# Revit family: Hager-UNIVERS-Surface_mounted-IP44-With_Cover-With_DIN-NoHosted-PL-pl
name_source: partatom
category: Electrical Equipment
units: mm (PartAtom-declared; Revit-internal decimal feet)

## family parameters
Always vertical = Yes
Cut with Voids When Loaded = No
Maintain Annotation Orientation = No
Panel Configuration = Two Columns, Circuits Across
Part Type = Panelboard
Room Calculation Point = No
Round Connector Dimension = Use Diameter
Shared = No
Work Plane-Based = Yes

## types (33) — shared parameters
Code hager = ADD-EC000214_EU
Default Elevation = 1200 mm
EF000007 - Kolor = Biały
EF000024 - Odporność na promieniowanie UV = No
EF000049 - Głębokość = 165 mm
EF000116 - Numer RAL = 9010
EF000118 - Z płytą montażową = No
EF000218 - Głębokość wbudowania = 161 mm  [stored 0.528215 ft]
EF001062 - Wykonanie zgodne z Dyrektywą Kompatybilności Elektromagnetycznej EMC = No
EF001088 - Możliwość rozbudowy = Yes
EF001134 - Szyna DIN = Yes
EF004462 - Rodzaj zamknięcia = Inne
EF005474 - Stopień ochrony (IP) = IP44
EF006244 - Transparentna pokrywa/drzwi = No
EF006306 - Z zamkiem = No
EF015941 - Drzwi przepuszczające sygnał = No
ETIM class code = EC000214
ETIM class name = Small distribution board
HG000002-with door or cover-pl = Yes
HG000003-Range-pl = UNIVERS
HG000005-Thickness-pl = 2 mm  [stored 0.00656168 ft]
HG000006-Flush mounted-pl = No
HG000011-Empty rows from bottom-pl = No
HG000012-Door swing angle-pl = 90.00°
HG000013-Door on the left-pl = No
HG000014-Door on the right-pl = Yes
HG000015-Clearance visibility-pl = Yes
HG000016-Door 3D visibility-pl = Yes
HG000017-Distance between poles-pl = 18 mm  [stored 0.0590551 ft]
HG000060-RAL-number = 9010
HG000099-Onfly Template ID-pl-PL = 507532
Manufacturer = Hager
Name BIM&CO = Electricity
Name hager = ADD_Enclosures_EC000214
Reference = Template-Enclosure_EU-EC000214
Uniformat = Low Tension Service & Dist.
Uniformat code = D501001
zero-valued in all types: EF001131 - Głębokość wewnętrzna, HG000007-Number of empty columns-pl

## per-type parameters (varying)
| type | BC_METADATA | EF000003 - Sposób montażu | EF000008 - Szerokość | EF000040 - Wysokość | EF000266 - Liczba rzędów | EF000332 - Wysokość wbudowania | EF000846 - Szerokość wbudowania | EF002950 - Szerokość wyrażona liczbą modułów | EF009212 - Wykonanie/rodzaj pokrywy | EF015776 - Listwa zaciskowa uziemienia | EF015777 - Listwa zaciskowa przewodu neutralnego | HG000001-Number of columns-pl | HG000004-Manufacturer reference-pl | HG000008-Number of empty rows-pl | HG000009-Double swing door-pl | HG000010-Asymmetric doors-pl | HGEF000266-Liczba rzędów | HGEF0002950-Szerokość wyrażona liczbą modułów |
| UNIVERS-Surface_mounted_W300_H500_D165_12_Modular_Spacing-FWB31S | {"ObjectGuid":"1e136a9b-75e4-4319-8c77-32bd0dc2c71d","ModelGuid":"185c7e43-76b0-4f0f-a409-50091b20c5eb","VariantGuid":"d1227972-96c4-41bb-bfb9-1cb3d9e40ddb","Revision":"#12","VariantName":"UNIVERS-Surface_mounted_W300_H500_D165_12_Modular_Spacing-FWB31S"} | Montaż natynkowy | 300 mm | 500 mm  [stored 1.64042 ft] | 3 | 500 mm  [stored 1.64042 ft] | 300 mm | 12 | Z otworem | Yes | Yes | 1 | FWB31S | 0 | No | No | 3 | 12 |
| UNIVERS-Surface_mounted_W550_H500_D165_26_Modular_Spacing-FWB32M2 | {"ObjectGuid":"1e136a9b-75e4-4319-8c77-32bd0dc2c71d","ModelGuid":"185c7e43-76b0-4f0f-a409-50091b20c5eb","VariantGuid":"1d3b936d-e440-496e-9ef6-1b36e04274c4","Revision":"#12","VariantName":"UNIVERS-Surface_mounted_W550_H500_D165_26_Modular_Spacing-FWB32M2"} | Montaż natynkowy | 550 mm | 500 mm  [stored 1.64042 ft] | 3 | 500 mm  [stored 1.64042 ft] | 550 mm | 26 | Zamknięty | No | No | 1 | FWB32M2 | 0 | No | No | 3 | 26 |
| UNIVERS-Surface_mounted_W550_H500_D165_24_Modular_Spacing-FWB32S | {"ObjectGuid":"1e136a9b-75e4-4319-8c77-32bd0dc2c71d","ModelGuid":"185c7e43-76b0-4f0f-a409-50091b20c5eb","VariantGuid":"2472cf2b-27e7-4fb8-9ea9-84f5d3778b47","Revision":"#12","VariantName":"UNIVERS-Surface_mounted_W550_H500_D165_24_Modular_Spacing-FWB32S"} | Montaż natynkowy | 550 mm | 500 mm  [stored 1.64042 ft] | 3 | 500 mm  [stored 1.64042 ft] | 550 mm | 24 | Z otworem | Yes | Yes | 2 | FWB32S | 0 | No | No | 3 | 24 |
| UNIVERS-Surface_mounted_W800_H500_D165_36_Modular_Spacing-FWB33S | {"ObjectGuid":"1e136a9b-75e4-4319-8c77-32bd0dc2c71d","ModelGuid":"185c7e43-76b0-4f0f-a409-50091b20c5eb","VariantGuid":"7aecc9d5-e5c1-440f-b2a3-c5abf14a60e6","Revision":"#12","VariantName":"UNIVERS-Surface_mounted_W800_H500_D165_36_Modular_Spacing-FWB33S"} | Montaż natynkowy | 800 mm  [stored 2.62467 ft] | 500 mm  [stored 1.64042 ft] | 3 | 500 mm  [stored 1.64042 ft] | 800 mm  [stored 2.62467 ft] | 36 | Z otworem | Yes | Yes | 3 | FWB33S | 0 | Yes | Yes | 3 | 36 |
| UNIVERS-Surface_mounted_W1050_H500_D165_48_Modular_Spacing-FWB34S | {"ObjectGuid":"1e136a9b-75e4-4319-8c77-32bd0dc2c71d","ModelGuid":"185c7e43-76b0-4f0f-a409-50091b20c5eb","VariantGuid":"d27bcc98-d304-4e4c-bd4b-80197513f53f","Revision":"#12","VariantName":"UNIVERS-Surface_mounted_W1050_H500_D165_48_Modular_Spacing-FWB34S"} | Montaż natynkowy | 1050 mm | 500 mm  [stored 1.64042 ft] | 3 | 500 mm  [stored 1.64042 ft] | 1050 mm | 48 | Z otworem | Yes | Yes | 4 | FWB34S | 0 | Yes | No | 3 | 48 |
| UNIVERS-Surface_mounted_W300_H650_D165_12_Modular_Spacing-FWB41S | {"ObjectGuid":"1e136a9b-75e4-4319-8c77-32bd0dc2c71d","ModelGuid":"185c7e43-76b0-4f0f-a409-50091b20c5eb","VariantGuid":"4b975c2e-89ce-482f-ad79-cb5683548a8a","Revision":"#12","VariantName":"UNIVERS-Surface_mounted_W300_H650_D165_12_Modular_Spacing-FWB41S"} | Montaż natynkowy | 300 mm | 650 mm  [stored 2.13255 ft] | 4 | 650 mm  [stored 2.13255 ft] | 300 mm | 12 | Z otworem | Yes | Yes | 1 | FWB41S | 0 | No | No | 4 | 12 |
| UNIVERS-Surface_mounted_W550_H650_D165_26_Modular_Spacing-FWB42M2 | {"ObjectGuid":"1e136a9b-75e4-4319-8c77-32bd0dc2c71d","ModelGuid":"185c7e43-76b0-4f0f-a409-50091b20c5eb","VariantGuid":"49d4ca06-d0b9-4d44-8aff-0f65a4984da5","Revision":"#12","VariantName":"UNIVERS-Surface_mounted_W550_H650_D165_26_Modular_Spacing-FWB42M2"} | Montaż natynkowy | 550 mm | 650 mm  [stored 2.13255 ft] | 4 | 650 mm  [stored 2.13255 ft] | 550 mm | 26 | Zamknięty | No | No | 1 | FWB42M2 | 0 | No | No | 4 | 26 |
| UNIVERS-Surface_mounted_W550_H650_D165_24_Modular_Spacing-FWB42S | {"ObjectGuid":"1e136a9b-75e4-4319-8c77-32bd0dc2c71d","ModelGuid":"185c7e43-76b0-4f0f-a409-50091b20c5eb","VariantGuid":"5138217c-8742-4b09-9714-137f47a1788c","Revision":"#12","VariantName":"UNIVERS-Surface_mounted_W550_H650_D165_24_Modular_Spacing-FWB42S"} | Natynkowy/podtynkowy | 550 mm | 650 mm  [stored 2.13255 ft] | 4 | 650 mm  [stored 2.13255 ft] | 550 mm | 24 | Z otworem | Yes | Yes | 2 | FWB42S | 0 | No | No | 4 | 24 |
| UNIVERS-Surface_mounted_W800_H650_D165_36_Modular_Spacing-FWB43S | {"ObjectGuid":"1e136a9b-75e4-4319-8c77-32bd0dc2c71d","ModelGuid":"185c7e43-76b0-4f0f-a409-50091b20c5eb","VariantGuid":"aa3dac15-5189-4800-92ae-ab21d3245b18","Revision":"#12","VariantName":"UNIVERS-Surface_mounted_W800_H650_D165_36_Modular_Spacing-FWB43S"} | Montaż natynkowy | 800 mm  [stored 2.62467 ft] | 650 mm  [stored 2.13255 ft] | 4 | 650 mm  [stored 2.13255 ft] | 800 mm  [stored 2.62467 ft] | 36 | Z otworem | Yes | Yes | 3 | FWB43S | 0 | Yes | Yes | 4 | 36 |
| UNIVERS-Surface_mounted_W1050_H650_D165_48_Modular_Spacing-FWB44S | {"ObjectGuid":"1e136a9b-75e4-4319-8c77-32bd0dc2c71d","ModelGuid":"185c7e43-76b0-4f0f-a409-50091b20c5eb","VariantGuid":"c1e77db2-3a83-4d34-876c-a818988fceb8","Revision":"#12","VariantName":"UNIVERS-Surface_mounted_W1050_H650_D165_48_Modular_Spacing-FWB44S"} | Montaż natynkowy | 1050 mm | 650 mm  [stored 2.13255 ft] | 4 | 650 mm  [stored 2.13255 ft] | 1050 mm | 48 | Z otworem | Yes | Yes | 4 | FWB44S | 0 | Yes | No | 4 | 48 |
| UNIVERS-Surface_mounted_W300_H800_D165_12_Modular_Spacing-FWB51S | {"ObjectGuid":"1e136a9b-75e4-4319-8c77-32bd0dc2c71d","ModelGuid":"185c7e43-76b0-4f0f-a409-50091b20c5eb","VariantGuid":"8deaed9d-0e43-4cd9-af4a-cd22cc333955","Revision":"#12","VariantName":"UNIVERS-Surface_mounted_W300_H800_D165_12_Modular_Spacing-FWB51S"} | Montaż natynkowy | 300 mm | 800 mm  [stored 2.62467 ft] | 5 | 800 mm  [stored 2.62467 ft] | 300 mm | 12 | Z otworem | Yes | Yes | 1 | FWB51S | 0 | No | No | 5 | 12 |
| UNIVERS-Surface_mounted_W550_H800_D165_26_Modular_Spacing-FWB52M2 | {"ObjectGuid":"1e136a9b-75e4-4319-8c77-32bd0dc2c71d","ModelGuid":"185c7e43-76b0-4f0f-a409-50091b20c5eb","VariantGuid":"49f808cc-c68f-41a3-9a95-eb34933de389","Revision":"#12","VariantName":"UNIVERS-Surface_mounted_W550_H800_D165_26_Modular_Spacing-FWB52M2"} | Montaż natynkowy | 550 mm | 800 mm  [stored 2.62467 ft] | 5 | 800 mm  [stored 2.62467 ft] | 550 mm | 26 | Zamknięty | No | No | 1 | FWB52M2 | 0 | No | No | 5 | 26 |
| UNIVERS-Surface_mounted_W550_H800_D165_24_Modular_Spacing-FWB52N | {"ObjectGuid":"1e136a9b-75e4-4319-8c77-32bd0dc2c71d","ModelGuid":"185c7e43-76b0-4f0f-a409-50091b20c5eb","VariantGuid":"3e297525-3ed2-4385-8154-3d3ab2640180","Revision":"#12","VariantName":"UNIVERS-Surface_mounted_W550_H800_D165_24_Modular_Spacing-FWB52N"} | Montaż natynkowy | 550 mm | 800 mm  [stored 2.62467 ft] | 5 | 800 mm  [stored 2.62467 ft] | 550 mm | 24 | Z otworem | No | No | 2 | FWB52N | 2 | No | No | 5 | 24 |
| UNIVERS-Surface_mounted_W550_H800_D165_24_Modular_Spacing-FWB52S | {"ObjectGuid":"1e136a9b-75e4-4319-8c77-32bd0dc2c71d","ModelGuid":"185c7e43-76b0-4f0f-a409-50091b20c5eb","VariantGuid":"01c9730f-b3d0-47a2-ac7a-2d98d1b4d2cc","Revision":"#12","VariantName":"UNIVERS-Surface_mounted_W550_H800_D165_24_Modular_Spacing-FWB52S"} | Montaż natynkowy | 550 mm | 800 mm  [stored 2.62467 ft] | 5 | 800 mm  [stored 2.62467 ft] | 550 mm | 24 | Z otworem | Yes | Yes | 2 | FWB52S | 0 | No | No | 5 | 24 |
| UNIVERS-Surface_mounted_W800_H800_D165_36_Modular_Spacing-FWB53N | {"ObjectGuid":"1e136a9b-75e4-4319-8c77-32bd0dc2c71d","ModelGuid":"185c7e43-76b0-4f0f-a409-50091b20c5eb","VariantGuid":"4d66ed62-46c3-48c6-b0b5-60542c6f606f","Revision":"#12","VariantName":"UNIVERS-Surface_mounted_W800_H800_D165_36_Modular_Spacing-FWB53N"} | Montaż natynkowy | 800 mm  [stored 2.62467 ft] | 800 mm  [stored 2.62467 ft] | 5 | 800 mm  [stored 2.62467 ft] | 800 mm  [stored 2.62467 ft] | 36 | Z otworem | No | No | 3 | FWB53N | 2 | Yes | Yes | 5 | 36 |
| UNIVERS-Surface_mounted_W800_H800_D165_36_Modular_Spacing-FWB53S | {"ObjectGuid":"1e136a9b-75e4-4319-8c77-32bd0dc2c71d","ModelGuid":"185c7e43-76b0-4f0f-a409-50091b20c5eb","VariantGuid":"ac522ccc-010b-47d7-9f1f-91c3f096dd22","Revision":"#12","VariantName":"UNIVERS-Surface_mounted_W800_H800_D165_36_Modular_Spacing-FWB53S"} | Montaż natynkowy | 800 mm  [stored 2.62467 ft] | 800 mm  [stored 2.62467 ft] | 5 | 800 mm  [stored 2.62467 ft] | 800 mm  [stored 2.62467 ft] | 36 | Z otworem | Yes | Yes | 3 | FWB53S | 0 | Yes | Yes | 5 | 36 |
| UNIVERS-Surface_mounted_W1050_H800_D165_48_Modular_Spacing-FWB54S | {"ObjectGuid":"1e136a9b-75e4-4319-8c77-32bd0dc2c71d","ModelGuid":"185c7e43-76b0-4f0f-a409-50091b20c5eb","VariantGuid":"e9c48e03-bc67-4c78-8834-0244d4d2a174","Revision":"#12","VariantName":"UNIVERS-Surface_mounted_W1050_H800_D165_48_Modular_Spacing-FWB54S"} | Montaż natynkowy | 1050 mm | 800 mm  [stored 2.62467 ft] | 5 | 800 mm  [stored 2.62467 ft] | 1050 mm | 48 | Z otworem | Yes | Yes | 4 | FWB54S | 0 | Yes | No | 5 | 48 |
| UNIVERS-Surface_mounted_W300_H950_D165_12_Modular_Spacing-FWB61S | {"ObjectGuid":"1e136a9b-75e4-4319-8c77-32bd0dc2c71d","ModelGuid":"185c7e43-76b0-4f0f-a409-50091b20c5eb","VariantGuid":"f680f3c5-64ea-4def-ba27-e1e1e8739d4a","Revision":"#12","VariantName":"UNIVERS-Surface_mounted_W300_H950_D165_12_Modular_Spacing-FWB61S"} | Montaż natynkowy | 300 mm | 950 mm  [stored 3.1168 ft] | 6 | 950 mm  [stored 3.1168 ft] | 300 mm | 12 | Z otworem | Yes | Yes | 1 | FWB61S | 0 | No | No | 6 | 12 |
| UNIVERS-Surface_mounted_W550_H950_D165_26_Modular_Spacing-FWB62M2 | {"ObjectGuid":"1e136a9b-75e4-4319-8c77-32bd0dc2c71d","ModelGuid":"185c7e43-76b0-4f0f-a409-50091b20c5eb","VariantGuid":"ad897574-3dc5-4a38-8937-7a40b74c3b45","Revision":"#12","VariantName":"UNIVERS-Surface_mounted_W550_H950_D165_26_Modular_Spacing-FWB62M2"} | Montaż natynkowy | 550 mm | 950 mm  [stored 3.1168 ft] | 6 | 950 mm  [stored 3.1168 ft] | 550 mm | 26 | Zamknięty | No | No | 1 | FWB62M2 | 0 | No | No | 6 | 26 |
| UNIVERS-Surface_mounted_W550_H950_D165_24_Modular_Spacing-FWB62N | {"ObjectGuid":"1e136a9b-75e4-4319-8c77-32bd0dc2c71d","ModelGuid":"185c7e43-76b0-4f0f-a409-50091b20c5eb","VariantGuid":"fb09d801-9a7a-4fa5-ba75-5b0c750c7af9","Revision":"#12","VariantName":"UNIVERS-Surface_mounted_W550_H950_D165_24_Modular_Spacing-FWB62N"} | Montaż natynkowy | 550 mm | 950 mm  [stored 3.1168 ft] | 6 | 950 mm  [stored 3.1168 ft] | 550 mm | 24 | Z otworem | No | No | 2 | FWB62N | 2 | No | No | 6 | 24 |
| UNIVERS-Surface_mounted_W550_H950_D165_24_Modular_Spacing-FWB62S | {"ObjectGuid":"1e136a9b-75e4-4319-8c77-32bd0dc2c71d","ModelGuid":"185c7e43-76b0-4f0f-a409-50091b20c5eb","VariantGuid":"ae616baf-cc23-4018-8f28-e766b632cec6","Revision":"#12","VariantName":"UNIVERS-Surface_mounted_W550_H950_D165_24_Modular_Spacing-FWB62S"} | Montaż natynkowy | 550 mm | 950 mm  [stored 3.1168 ft] | 6 | 950 mm  [stored 3.1168 ft] | 550 mm | 24 | Z otworem | Yes | Yes | 2 | FWB62S | 0 | No | No | 6 | 24 |
| UNIVERS-Surface_mounted_W800_H950_D165_36_Modular_Spacing-FWB63N | {"ObjectGuid":"1e136a9b-75e4-4319-8c77-32bd0dc2c71d","ModelGuid":"185c7e43-76b0-4f0f-a409-50091b20c5eb","VariantGuid":"b47fe18c-d61f-4981-abfc-ed10af9d808b","Revision":"#12","VariantName":"UNIVERS-Surface_mounted_W800_H950_D165_36_Modular_Spacing-FWB63N"} | Montaż natynkowy | 800 mm  [stored 2.62467 ft] | 950 mm  [stored 3.1168 ft] | 6 | 950 mm  [stored 3.1168 ft] | 800 mm  [stored 2.62467 ft] | 36 | Z otworem | No | No | 3 | FWB63N | 2 | Yes | Yes | 6 | 36 |
| UNIVERS-Surface_mounted_W800_H950_D165_36_Modular_Spacing-FWB63S | {"ObjectGuid":"1e136a9b-75e4-4319-8c77-32bd0dc2c71d","ModelGuid":"185c7e43-76b0-4f0f-a409-50091b20c5eb","VariantGuid":"1141f038-8ff0-4ac4-9620-b47aa2759a1b","Revision":"#12","VariantName":"UNIVERS-Surface_mounted_W800_H950_D165_36_Modular_Spacing-FWB63S"} | Montaż natynkowy | 800 mm  [stored 2.62467 ft] | 950 mm  [stored 3.1168 ft] | 6 | 950 mm  [stored 3.1168 ft] | 800 mm  [stored 2.62467 ft] | 36 | Z otworem | Yes | Yes | 3 | FWB63S | 0 | Yes | Yes | 6 | 36 |
| UNIVERS-Surface_mounted_W1050_H950_D165_48_Modular_Spacing-FWB64N | {"ObjectGuid":"1e136a9b-75e4-4319-8c77-32bd0dc2c71d","ModelGuid":"185c7e43-76b0-4f0f-a409-50091b20c5eb","VariantGuid":"2bac9421-bbbb-4d50-a78b-28f0cf8483d5","Revision":"#12","VariantName":"UNIVERS-Surface_mounted_W1050_H950_D165_48_Modular_Spacing-FWB64N"} | Montaż natynkowy | 1050 mm | 950 mm  [stored 3.1168 ft] | 6 | 950 mm  [stored 3.1168 ft] | 1050 mm | 48 | Z otworem | No | No | 4 | FWB64N | 2 | Yes | No | 6 | 48 |
| UNIVERS-Surface_mounted_W1050_H950_D165_48_Modular_Spacing-FWB64S | {"ObjectGuid":"1e136a9b-75e4-4319-8c77-32bd0dc2c71d","ModelGuid":"185c7e43-76b0-4f0f-a409-50091b20c5eb","VariantGuid":"e5692b63-8863-473f-9759-d0b30e535f3d","Revision":"#12","VariantName":"UNIVERS-Surface_mounted_W1050_H950_D165_48_Modular_Spacing-FWB64S"} | Montaż natynkowy | 1050 mm | 950 mm  [stored 3.1168 ft] | 6 | 950 mm  [stored 3.1168 ft] | 1050 mm | 48 | Z otworem | Yes | Yes | 4 | FWB64S | 0 | Yes | No | 6 | 48 |
| UNIVERS-Surface_mounted_W300_H1100_D165_12_Modular_Spacing-FWB71S | {"ObjectGuid":"1e136a9b-75e4-4319-8c77-32bd0dc2c71d","ModelGuid":"185c7e43-76b0-4f0f-a409-50091b20c5eb","VariantGuid":"67287efe-4212-4747-a39f-5053eb7a172f","Revision":"#12","VariantName":"UNIVERS-Surface_mounted_W300_H1100_D165_12_Modular_Spacing-FWB71S"} | Montaż natynkowy | 300 mm | 1100 mm | 7 | 1100 mm | 300 mm | 12 | Z otworem | Yes | Yes | 1 | FWB71S | 0 | No | No | 7 | 12 |
| UNIVERS-Surface_mounted_W550_H1100_D165_26_Modular_Spacing-FWB72M2 | {"ObjectGuid":"1e136a9b-75e4-4319-8c77-32bd0dc2c71d","ModelGuid":"185c7e43-76b0-4f0f-a409-50091b20c5eb","VariantGuid":"2c7a3ac6-8412-4914-8f4a-ff8640724605","Revision":"#12","VariantName":"UNIVERS-Surface_mounted_W550_H1100_D165_26_Modular_Spacing-FWB72M2"} | Montaż natynkowy | 550 mm | 1100 mm | 7 | 1100 mm | 550 mm | 26 | Zamknięty | No | No | 1 | FWB72M2 | 0 | No | No | 7 | 26 |
| UNIVERS-Surface_mounted_W550_H1100_D165_24_Modular_Spacing-FWB72N | {"ObjectGuid":"1e136a9b-75e4-4319-8c77-32bd0dc2c71d","ModelGuid":"185c7e43-76b0-4f0f-a409-50091b20c5eb","VariantGuid":"81afa6e8-26ce-45af-a25c-4ba68814763f","Revision":"#12","VariantName":"UNIVERS-Surface_mounted_W550_H1100_D165_24_Modular_Spacing-FWB72N"} | Montaż natynkowy | 550 mm | 1100 mm | 7 | 1100 mm | 550 mm | 24 | Z otworem | No | No | 2 | FWB72N | 2 | No | No | 7 | 24 |
| UNIVERS-Surface_mounted_W550_H1100_D165_24_Modular_Spacing-FWB72S | {"ObjectGuid":"1e136a9b-75e4-4319-8c77-32bd0dc2c71d","ModelGuid":"185c7e43-76b0-4f0f-a409-50091b20c5eb","VariantGuid":"452d8680-f7aa-4557-a09a-31c66ab7cda8","Revision":"#12","VariantName":"UNIVERS-Surface_mounted_W550_H1100_D165_24_Modular_Spacing-FWB72S"} | Natynkowy/podtynkowy | 550 mm | 1100 mm | 7 | 1100 mm | 550 mm | 24 | Z otworem | Yes | Yes | 2 | FWB72S | 0 | No | No | 7 | 24 |
| UNIVERS-Surface_mounted_W800_H1100_D165_36_Modular_Spacing-FWB73N | {"ObjectGuid":"1e136a9b-75e4-4319-8c77-32bd0dc2c71d","ModelGuid":"185c7e43-76b0-4f0f-a409-50091b20c5eb","VariantGuid":"66f246f6-d4a0-4979-a03b-ea0ab66e612f","Revision":"#12","VariantName":"UNIVERS-Surface_mounted_W800_H1100_D165_36_Modular_Spacing-FWB73N"} | Montaż natynkowy | 800 mm  [stored 2.62467 ft] | 1100 mm | 7 | 1100 mm | 800 mm  [stored 2.62467 ft] | 36 | Z otworem | No | No | 3 | FWB73N | 2 | Yes | Yes | 7 | 36 |
| UNIVERS-Surface_mounted_W800_H1100_D165_36_Modular_Spacing-FWB73S | {"ObjectGuid":"1e136a9b-75e4-4319-8c77-32bd0dc2c71d","ModelGuid":"185c7e43-76b0-4f0f-a409-50091b20c5eb","VariantGuid":"67f3c783-74fb-4fdd-91eb-cf8c36cf74f4","Revision":"#12","VariantName":"UNIVERS-Surface_mounted_W800_H1100_D165_36_Modular_Spacing-FWB73S"} | Natynkowy/podtynkowy | 800 mm  [stored 2.62467 ft] | 1100 mm | 7 | 1100 mm | 800 mm  [stored 2.62467 ft] | 36 | Z otworem | Yes | Yes | 3 | FWB73S | 0 | Yes | Yes | 7 | 36 |
| UNIVERS-Surface_mounted_W1050_H1100_D165_48_Modular_Spacing-FWB74N | {"ObjectGuid":"1e136a9b-75e4-4319-8c77-32bd0dc2c71d","ModelGuid":"185c7e43-76b0-4f0f-a409-50091b20c5eb","VariantGuid":"9159eeb7-d08b-42c1-bc51-3c43f1eafb86","Revision":"#12","VariantName":"UNIVERS-Surface_mounted_W1050_H1100_D165_48_Modular_Spacing-FWB74N"} | Montaż natynkowy | 1050 mm | 1100 mm | 7 | 1100 mm | 1050 mm | 48 | Z otworem | No | No | 4 | FWB74N | 2 | Yes | No | 7 | 48 |
| UNIVERS-Surface_mounted_W1050_H1100_D165_48_Modular_Spacing-FWB74S | {"ObjectGuid":"1e136a9b-75e4-4319-8c77-32bd0dc2c71d","ModelGuid":"185c7e43-76b0-4f0f-a409-50091b20c5eb","VariantGuid":"8ccc5688-af0e-483f-90f3-193314103cd9","Revision":"#12","VariantName":"UNIVERS-Surface_mounted_W1050_H1100_D165_48_Modular_Spacing-FWB74S"} | Natynkowy/podtynkowy | 1050 mm | 1100 mm | 7 | 1100 mm | 1050 mm | 48 | Z otworem | Yes | Yes | 4 | FWB74S | 0 | Yes | No | 7 | 48 |

note: [stored X ft] marks values corroborated as IEEE doubles in the binary element streams (Revit-internal decimal feet)

## geometry (parser evidence)
native form markers: Sweep x14
no freeform markers — native parametric forms only
